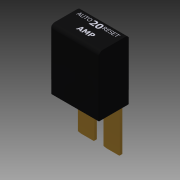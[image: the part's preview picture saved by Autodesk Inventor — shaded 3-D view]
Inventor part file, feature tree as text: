
AUTODESK INVENTOR PART (.ipt)
format: ipt  version: 2016 SP1 (Build 200210100, 210)  size: 451,584 bytes
history: native  units: in
note: dims shown in document units (in); Inventor stores cm internally (conversion verified against a paired STEP export)
features: sketch x6, extrude x4, plane x3, emboss x2, fillet x1, mirror x1
ambient origin geometry x8: Origin, YZ Plane, XZ Plane, XY Plane, X Axis, Y Axis, Z Axis, Center Point
bodies: Solid1 (feature_tree)
feature tree (17):
  extrude  "Extrusion1"  Depth=0.39in
  fillet  "Fillet1"  Radius=0.78in
  extrude  "Extrusion3"  Depth=0.212in
  extrude  "Extrusion4"  Depth=0.0585in
  extrude  "Extrusion5"  Depth=0.57in TaperAngle=0.0deg
  plane  "Work Plane1"
  mirror  "Mirror1"
  plane  "Work Plane2"
  emboss  "Emboss1"
  plane  "Work Plane4"
  emboss  "Emboss3"
  sketch  "Sketch1"  dims[d0=0.62in d1=0.39in d2=0.78in d3=0.0in]
  sketch  "Sketch2"  dims[d4=0.01in d5=0.05in d6=0.212in]
  sketch  "Sketch3"  dims[d8=0.031in d13=0.0585in]
  sketch  "Sketch4"  dims[d14=0.57in d15=0.0in d16=0.57in d17=0.0in]
  sketch  "Sketch6"  dims[d18=0.023in]
  sketch  "Sketch8"  dims[d19=0.023in d20=0.023in d21=0.57in d22=0.0in d26=0.1875in d27=0.0001in d28=0.0in d32=0.1875in d33=0.0001in d34=0.0in]
